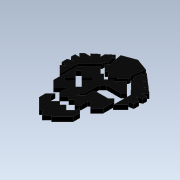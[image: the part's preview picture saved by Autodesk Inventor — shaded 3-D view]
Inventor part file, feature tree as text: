
AUTODESK INVENTOR PART (.ipt)
format: ipt  version: 2020 (Build 240168000, 168)  size: 565,760 bytes
history: native  units: in
note: dims shown in document units (in); Inventor stores cm internally (conversion verified against a paired STEP export)
features: extrude x6, projected_geometry x5, sketch x4
ambient origin geometry x8: Origin, YZ Plane, XZ Plane, XY Plane, X Axis, Y Axis, Z Axis, Center Point
bodies: Solid1 (feature_tree)
feature tree (15):
  extrude  "Extrusion1"  TaperAngle=90.0deg  [1 undecoded]
  sketch  "Sketch2"  dims[d2=45.0deg d3=0.0394in]
  extrude  "Extrusion2"  Depth=0.0394in
  extrude  "Extrusion3"  TaperAngle=90.0deg  [1 undecoded]
  sketch  "Sketch3"  dims[d4=0.5906in d5=90.0deg]
  extrude  "Extrusion4"  Depth=0.5906in
  extrude  "Extrusion5"  TaperAngle=90.0deg  [1 undecoded]
  extrude  "Extrusion6"  Depth=0.1969in
  sketch  "Sketch1"  dims[d0=0.3937in d1=90.0deg]
  projected_geometry  "Projected Loop1"
  projected_geometry  "Projected Loop2"
  projected_geometry  "Projected Loop3"
  sketch  "Sketch4"  dims[d6=0.3937in d7=0.5906in d8=90.0deg d9=0.1969in d10=0.3937in d11=45.0deg d12=0.5906in d13=0.3937in d14=45.0deg d15=0.5906in d16=90.0deg d17=0.3937in d18=90.0deg d19=0.3937in d20=90.0deg d21=0.5906in d22=90.0deg d23=0.5906in d24=90.0deg d25=0.5906in d26=0.5906in d27=0.3937in d28=0.5906in d29=45.0deg d30=0.5906in d31=45.0deg d32=0.3937in d33=0.5906in d34=135.0deg d35=1.1811in d36=1.1811in d37=135.0deg d38=0.1969in d39=135.0deg d40=90.0deg d41=0.7874in d42=0.1969in d43=0.7874in d44=135.0deg d45=0.1969in d46=0.4331in d47=0.1969in d48=45.0deg d49=0.1969in d50=90.0deg d51=0.7874in d52=0.7874in d53=90.0deg d54=0.5906in d55=0.5906in d56=0.1969in d57=135.0deg d58=0.7297in d59=0.3937in d60=0.3937in d61=45.0deg d62=45.0deg d63=0.1532in d64=0.1969in d65=0.1969in d66=0.7874in d67=0.4752in d68=135.0deg d69=0.9843in d70=135.0deg d71=0.3868in d72=0.3937in d73=135.0deg d74=0.3937in d75=135.0deg d76=90.0deg d77=0.689in d78=0.689in d79=1.0827in d80=1.0827in d81=3.937in d82=135.0deg d83=45.0deg d84=1.1832in d85=1.1832in d86=90.0deg d87=0.5906in d88=5.4304in d89=2.6102in d90=0.1462in d91=0.8608in d92=0.7129in d93=3.8974in d94=0.1969in d95=0.4524in d96=0.4524in d97=0.1969in d98=0.1969in d99=45.0deg d100=0.5906in d101=45.0deg d102=0.5906in d103=90.0deg d104=0.1968in d105=90.0deg d106=0.7087in d107=0.7087in d108=2.7839in d109=0.1969in d110=0.1969in d111=0.1969in d112=135.0deg d113=135.0deg d114=0.1969in d115=1.1811in d116=0.8589in d117=0.6871in d118=1.2598in d119=0.8589in d120=1.1811in d121=0.6871in d122=0.3937in d123=0.0in d124=0.3937in d125=0.0in d126=0.3937in d127=0.0in d128=0.5906in d129=0.3937in d130=0.0in d131=0.3937in d132=0.0in d133=0.1969in d134=0.1253in d135=0.1253in d136=1.5748in d137=45.0deg d138=1.1811in d139=1.5748in d140=2.5591in d141=0.0in d142=0.5655in d143=0.6519in d144=0.1274in d145=3.6191in d146=4.1414in d147=4.6511in d148=2.4918in d149=1.9526in d150=0.696in d151=1.8156in d152=0.8886in d153=1.3372in d154=2.5899in d155=4.4186in d156=4.9648in d157=0.3937in d158=0.0in d159=0.0197in d160=0.0344in]
  projected_geometry  "Projected Loop4"
  projected_geometry  "Projected Loop5"
note: 3 required parameter values undecoded (feature->parameter linkage not recoverable at this tier; creation-order binding heuristic only, values carry confidence <= 0.55)
